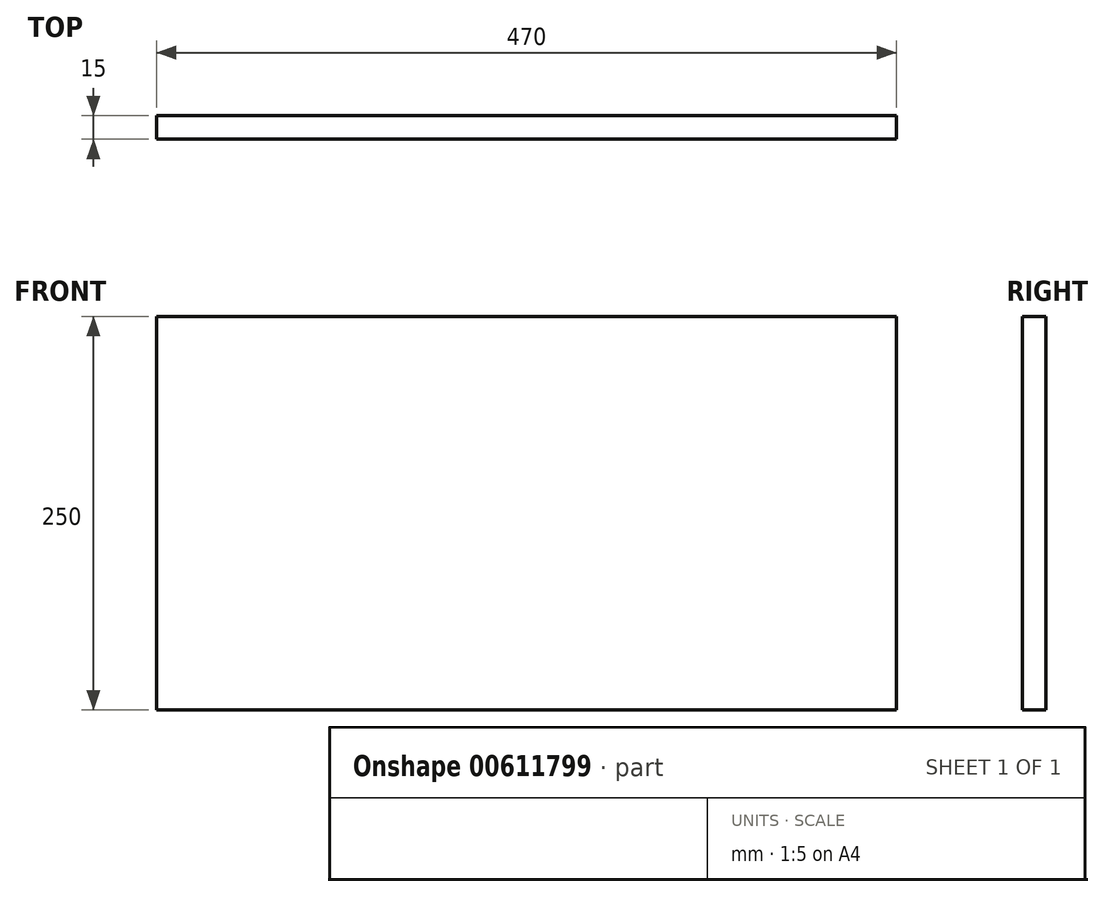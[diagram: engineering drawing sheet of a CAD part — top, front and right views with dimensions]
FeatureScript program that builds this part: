
annotation { "Feature Type Name" : "Feature", "Feature Type Description" : "" }
export const myFeature = defineFeature(function(context is Context, id is Id, definition is map)
    precondition{}
    {
        {
            var Q0;
            Q0=qCreatedBy(makeId("Front.planeOp"),FACE);
            var sketch = newSketch(context, id + "F0", { "sketchPlane" : qUnion([Q0])});
            skLineSegment(sketch, "E0.bottom", {"start": v(-235, 125) * mm, "end": v(235, 125) * mm});
            skLineSegment(sketch, "E0.top", {"start": v(-235, -125) * mm, "end": v(235, -125) * mm});
            skLineSegment(sketch, "E0.left", {"start": v(-235, 125) * mm, "end": v(-235, -125) * mm});
            skLineSegment(sketch, "E0.right", {"start": v(235, 125) * mm, "end": v(235, -125) * mm});
            skPoint(sketch, "E0.middle", {"position": v(0, 0) * mm});
            skSolve(sketch);
        }
        {
            var Q0;
            Q0=qSketchRegion(id+"F0",true);
            extrude(context, id + "F1", {"entities" : qUnion([Q0]), "depth" : 15 * mm, "offsetDistance" : 25 * mm});
        }
    });
